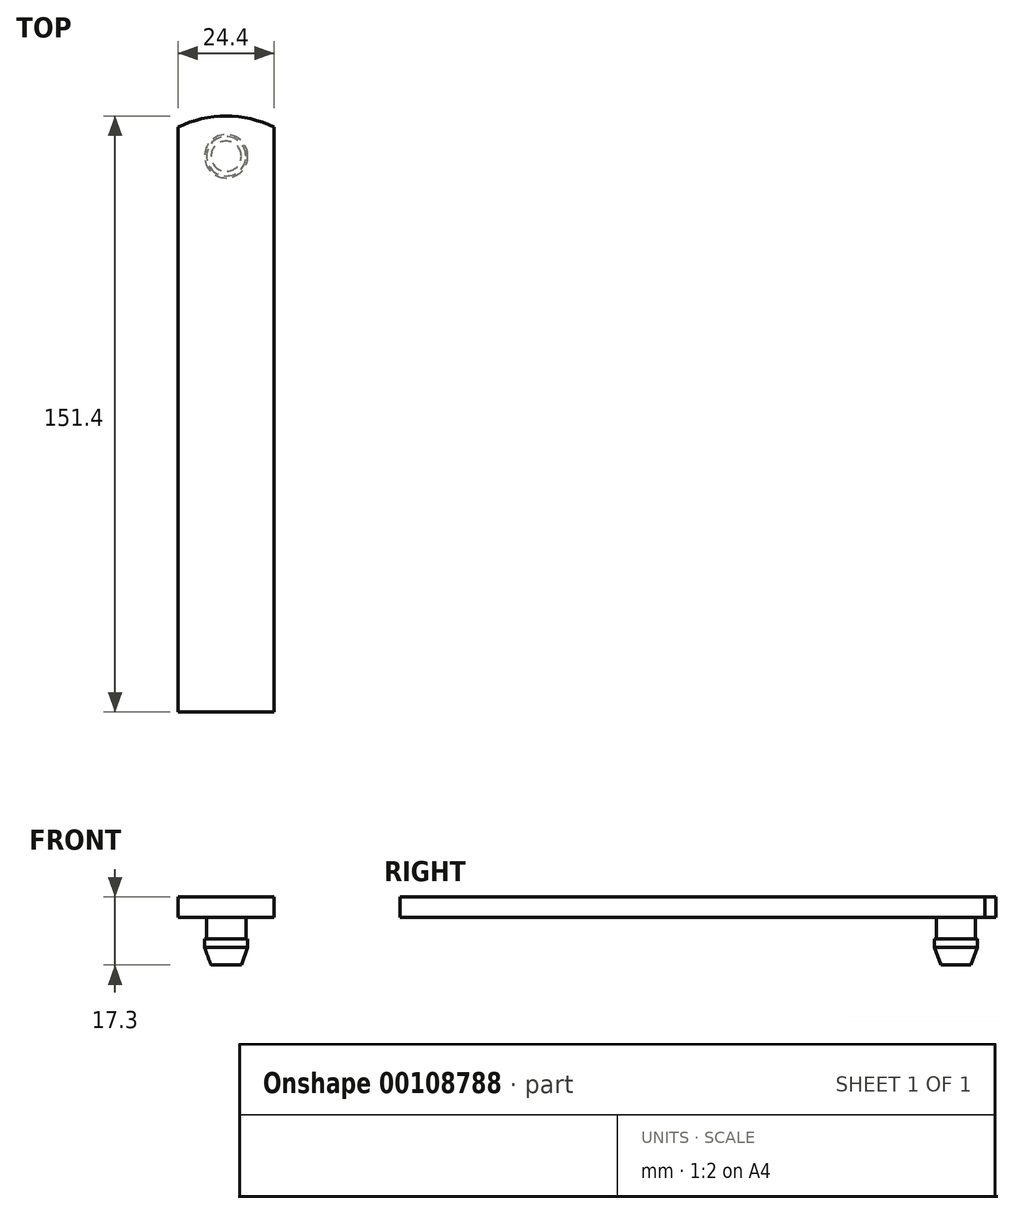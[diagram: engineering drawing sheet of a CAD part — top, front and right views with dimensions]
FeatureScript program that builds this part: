
annotation { "Feature Type Name" : "Feature", "Feature Type Description" : "" }
export const myFeature = defineFeature(function(context is Context, id is Id, definition is map)
    precondition{}
    {
        {
            var Q0;
            Q0=qCreatedBy(makeId("Top.planeOp"),FACE);
            var sketch = newSketch(context, id + "F0", { "sketchPlane" : qUnion([Q0])});
            skLineSegment(sketch, "E0", {"start": v(0, 0) * mm, "end": v(-12.2, 0) * mm});
            skLineSegment(sketch, "E1", {"start": v(-12.2, 0) * mm, "end": v(-12.2, 148.6) * mm});
            skLineSegment(sketch, "E2", {"start": v(0, 0) * mm, "end": v(12.2, 0) * mm});
            skLineSegment(sketch, "E3", {"start": v(12.2, 0) * mm, "end": v(12.2, 148.6) * mm});
            skLineSegment(sketch, "E4", {"start": v(-12.2, 148.6) * mm, "end": v(12.2, 148.6) * mm});
            skPoint(sketch, "E5.endSnap0", {"position": v(0, 148.6) * mm});
            skArc(sketch, "E6", {"start": v(12.2, 148.6) * mm, "mid": v(0, 151.4) * mm, "end": v(-12.2, 148.6) * mm});
            skLineSegment(sketch, "E7", {"start": v(0, 148.6) * mm, "end": v(0, 151.4) * mm});
            skSolve(sketch);
        }
        {
            var Q0;
            Q0=makeQuery(id+"F0.imprint","IMPRINT",FACE,{"disambiguationData":[TD([[makeQuery(id+"F0.imprint","IMPRINT",EDGE,{"derivedFrom":sQuery(id+"F0.wireOp",EDGE,"E0")}),-1.0]])]});
            var Q1;
            {var subQ3=sQuery(id+"F0.wireOp",EDGE,"E7");Q1=makeQuery(id+"F0.imprint","IMPRINT",FACE,{"disambiguationData":[TD([[makeQuery(id+"F0.imprint","IMPRINT",EDGE,{"derivedFrom":subQ3}),-1.0]])]});}
            var Q2;
            {var subQ3=sQuery(id+"F0.wireOp",EDGE,"E7");Q2=makeQuery(id+"F0.imprint","IMPRINT",FACE,{"disambiguationData":[TD([[makeQuery(id+"F0.imprint","IMPRINT",EDGE,{"derivedFrom":subQ3}),1.0]])]});}
            extrude(context, id + "F1", {"entities" : qUnion([Q0, Q1, Q2]), "oppositeDirection" : true, "depth" : 5.2 * mm});
        }
        {
            var Q0;
            Q0=makeQuery(id+"F1.opExtrude","CAP_FACE",FACE,{"disambiguationData":[OSD([sQuery(id+"F0.wireOp",EDGE,"E0"),sQuery(id+"F0.wireOp",EDGE,"E1"),sQuery(id+"F0.wireOp",EDGE,"E2"),sQuery(id+"F0.wireOp",EDGE,"E3"),sQuery(id+"F0.wireOp",EDGE,"E6")])],"isStart":false});
            var sketch = newSketch(context, id + "F2", { "sketchPlane" : qUnion([Q0])});
            skPoint(sketch, "E8.endSnap0", {"position": v(0, -151.4) * mm});
            skPoint(sketch, "E9", {"position": v(0, -141.2) * mm});
            skCircle(sketch, "E10", {"center": v(0, -141.2) * mm, "radius": 5 * mm});
            skPoint(sketch, "E11", {"position": v(0, 0) * mm});
            skLineSegment(sketch, "E12", {"start": v(12.2, -148.6) * mm, "end": v(-12.2, -148.6) * mm});
            skPoint(sketch, "E13", {"position": v(0, -136.2) * mm});
            skSolve(sketch);
        }
        {
            var Q0;
            Q0 = qSketchRegion(id + "F2", true);
            extrude(context, id + "F3", {"entities" : qUnion([Q0]), "operationType" : NewBodyOperationType.ADD, "depth" : 5.4 * mm});
        }
        {
            var Q0;
            Q0=makeQuery(id+"F3.opExtrude","CAP_FACE",FACE,{"disambiguationData":[OSD([sQuery(id+"F2.wireOp",EDGE,"E10")])],"isStart":false});
            cPlane(context, id + "F4", {"entities" : qUnion([Q0]), "cplaneType" : CPlaneType.OFFSET, "offset" : 0 * mm, "width" : 150 * mm, "height" : 150 * mm});
        }
        {
            var Q0;
            Q0=qCreatedBy(id+"F4.planeOp",FACE);
            var sketch = newSketch(context, id + "F5", { "sketchPlane" : qUnion([Q0])});
            skCircle(sketch, "E14", {"center": v(0, -141.2) * mm, "radius": 5.5 * mm});
            skSolve(sketch);
        }
        {
            var Q0;
            Q0 = qSketchRegion(id + "F5", true);
            extrude(context, id + "F6", {"entities" : qUnion([Q0]), "operationType" : NewBodyOperationType.ADD, "depth" : 2.2 * mm});
        }
        {
            var Q0;
            Q0=makeQuery(id+"F6.opExtrude","CAP_FACE",FACE,{"disambiguationData":[OSD([sQuery(id+"F5.wireOp",EDGE,"E14")])],"isStart":false});
            cPlane(context, id + "F7", {"entities" : qUnion([Q0]), "cplaneType" : CPlaneType.OFFSET, "offset" : 4.5 * mm, "width" : 150 * mm, "height" : 150 * mm});
        }
        {
            var Q0;
            Q0=qCreatedBy(id+"F7.planeOp",FACE);
            var sketch = newSketch(context, id + "F8", { "sketchPlane" : qUnion([Q0])});
            skCircle(sketch, "E15", {"center": v(0, -141.2) * mm, "radius": 3.85 * mm});
            skSolve(sketch);
        }
        {
            var Q0;
            Q0=makeQuery(id+"F6.opExtrude","CAP_FACE",FACE,{"disambiguationData":[OSD([sQuery(id+"F5.wireOp",EDGE,"E14")])],"isStart":false});
            cPlane(context, id + "F9", {"entities" : qUnion([Q0]), "cplaneType" : CPlaneType.OFFSET, "offset" : 0 * mm, "width" : 150 * mm, "height" : 150 * mm});
        }
        {
            var Q0;
            Q0=qCreatedBy(id+"F9.planeOp",FACE);
            var sketch = newSketch(context, id + "F10", { "sketchPlane" : qUnion([Q0])});
            skCircle(sketch, "E16.0", {"center": v(0, -141.2) * mm, "radius": 5.5 * mm});
            skSolve(sketch);
        }
        {
            var Q1;
            Q1=makeQuery(id+"F10.imprint","IMPRINT",FACE,{"disambiguationData":[TD([[makeQuery(id+"F10.imprint","IMPRINT",EDGE,{"derivedFrom":sQuery(id+"F10.wireOp",EDGE,"E16.0")}),1.0]])]});
            var Q2;
            Q2=makeQuery(id+"F8.imprint","IMPRINT",FACE,{"disambiguationData":[TD([[makeQuery(id+"F8.imprint","IMPRINT",EDGE,{"derivedFrom":sQuery(id+"F8.wireOp",EDGE,"E15")}),1.0]])]});
            loft(context, id + "F11", {"operationType" : NewBodyOperationType.ADD, "sheetProfilesArray" : [{ "sheetProfileEntities" : qUnion([Q1]) }, { "sheetProfileEntities" : qUnion([Q2]) }]});
        }
        {
            var Q0;
            Q0=makeQuery(id+"F1.opExtrude","SWEPT_FACE",FACE,{"disambiguationData":[OSD([sQuery(id+"F0.wireOp",EDGE,"E3")])]});
            cPlane(context, id + "F12", {"entities" : qUnion([Q0]), "cplaneType" : CPlaneType.OFFSET, "offset" : 0 * mm, "width" : 150 * mm, "height" : 150 * mm});
        }
    });
